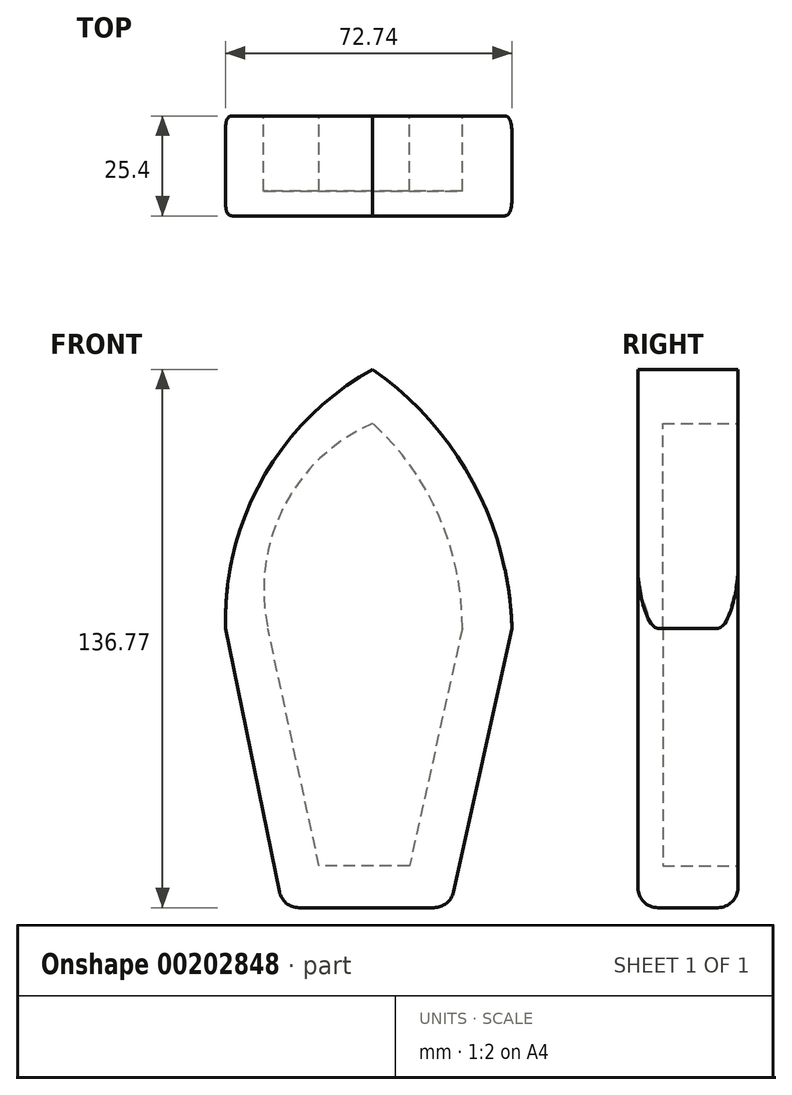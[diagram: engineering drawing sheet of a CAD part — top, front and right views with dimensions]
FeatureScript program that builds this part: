
annotation { "Feature Type Name" : "Feature", "Feature Type Description" : "" }
export const myFeature = defineFeature(function(context is Context, id is Id, definition is map)
    precondition{}
    {
        {
            var Q0;
            Q0=qCreatedBy(makeId("Front.planeOp"),FACE);
            var sketch = newSketch(context, id + "F0", { "sketchPlane" : qUnion([Q0])});
            skArc(sketch, "E0", {"start": v(0, 65.78) * mm, "mid": v(-27.87, 38.12) * mm, "end": v(-37.3, 0) * mm});
            skArc(sketch, "E1", {"start": v(35.4, 0) * mm, "mid": v(25.52, 37.1) * mm, "end": v(0, 65.78) * mm});
            skLineSegment(sketch, "E2", {"start": v(-37.3, 0) * mm, "end": v(-22.86, -71) * mm});
            skLineSegment(sketch, "E3", {"start": v(35.4, 0) * mm, "end": v(19.65, -71) * mm});
            skLineSegment(sketch, "E4", {"start": v(-22.86, -71) * mm, "end": v(19.65, -71) * mm});
            skSolve(sketch);
        }
        {
            var Q0;
            Q0=makeQuery(id+"F0.imprint","IMPRINT",FACE,{"disambiguationData":[TD([[makeQuery(id+"F0.imprint","IMPRINT",EDGE,{"derivedFrom":sQuery(id+"F0.wireOp",EDGE,"E0")}),1.0]])]});
            extrude(context, id + "F1", {"entities" : qUnion([Q0]), "depth" : 25.4 * mm});
        }
        {
            var Q0;
            Q0=makeQuery(id+"F1.opExtrude","CAP_FACE",FACE,{"disambiguationData":[OSD([sQuery(id+"F0.wireOp",EDGE,"E0"),sQuery(id+"F0.wireOp",EDGE,"E1"),sQuery(id+"F0.wireOp",EDGE,"E2"),sQuery(id+"F0.wireOp",EDGE,"E3"),sQuery(id+"F0.wireOp",EDGE,"E4")])],"isStart":true});
            var sketch = newSketch(context, id + "F2", { "sketchPlane" : qUnion([Q0])});
            skArc(sketch, "E5", {"start": v(0, 52.07) * mm, "mid": v(-16.92, 28.45) * mm, "end": v(-22.78, 0) * mm});
            skLineSegment(sketch, "E6", {"start": v(-22.78, 0) * mm, "end": v(-9.38, -60.43) * mm});
            skLineSegment(sketch, "E7", {"start": v(-9.38, -60.43) * mm, "end": v(13.56, -60.43) * mm});
            skLineSegment(sketch, "E8", {"start": v(13.56, -60.43) * mm, "end": v(26.62, 0) * mm});
            skArc(sketch, "E9", {"start": v(26.62, 0) * mm, "mid": v(22.6, 30.78) * mm, "end": v(0, 52.07) * mm});
            skSolve(sketch);
        }
        {
            var Q0;
            Q0=makeQuery(id+"F2.imprint","IMPRINT",FACE,{"disambiguationData":[TD([[makeQuery(id+"F2.imprint","IMPRINT",EDGE,{"derivedFrom":sQuery(id+"F2.wireOp",EDGE,"E5")}),1.0]])]});
            extrude(context, id + "F3", {"entities" : qUnion([Q0]), "operationType" : NewBodyOperationType.REMOVE, "depth" : 19.05 * mm});
        }
        {
            var Q0;
            Q0 = qSketchRegion(id + "F2", true);
            extrude(context, id + "F4", {"entities" : qUnion([Q0]), "operationType" : NewBodyOperationType.REMOVE, "oppositeDirection" : true, "depth" : 19.05 * mm});
        }
        {
            var Q0;
            Q0=makeQuery(id+"F1.opExtrude","CAP_EDGE",EDGE,{"disambiguationData":[OSD([sQuery(id+"F0.wireOp",EDGE,"E3")])],"isStart":true});
            var Q1;
            Q1=makeQuery(id+"F1.opExtrude","CAP_EDGE",EDGE,{"disambiguationData":[OSD([sQuery(id+"F0.wireOp",EDGE,"E3")])],"isStart":false});
            var Q2;
            Q2=makeQuery(id+"F1.opExtrude","SWEPT_EDGE",EDGE,{"disambiguationData":[OSD([sQuery(id+"F0.wireOp",EDGE,"E3"),sQuery(id+"F0.wireOp",EDGE,"E4")])]});
            var Q3;
            Q3=makeQuery(id+"F1.opExtrude","CAP_EDGE",EDGE,{"disambiguationData":[OSD([sQuery(id+"F0.wireOp",EDGE,"E4")])],"isStart":true});
            var Q4;
            Q4=makeQuery(id+"F1.opExtrude","CAP_EDGE",EDGE,{"disambiguationData":[OSD([sQuery(id+"F0.wireOp",EDGE,"E4")])],"isStart":false});
            var Q5;
            Q5=makeQuery(id+"F1.opExtrude","SWEPT_EDGE",EDGE,{"disambiguationData":[OSD([sQuery(id+"F0.wireOp",EDGE,"E2"),sQuery(id+"F0.wireOp",EDGE,"E4")])]});
            var Q6;
            Q6=makeQuery(id+"F1.opExtrude","CAP_EDGE",EDGE,{"disambiguationData":[OSD([sQuery(id+"F0.wireOp",EDGE,"E2")])],"isStart":true});
            var Q7;
            Q7=makeQuery(id+"F1.opExtrude","CAP_EDGE",EDGE,{"disambiguationData":[OSD([sQuery(id+"F0.wireOp",EDGE,"E2")])],"isStart":false});
            fillet(context, id + "F5", {"entities" : qUnion([Q0, Q1, Q2, Q3, Q4, Q5, Q6, Q7]), "radius" : 5.08 * mm, "tangentPropagation" : true, "allowEdgeOverflow" : false});
        }
    });
